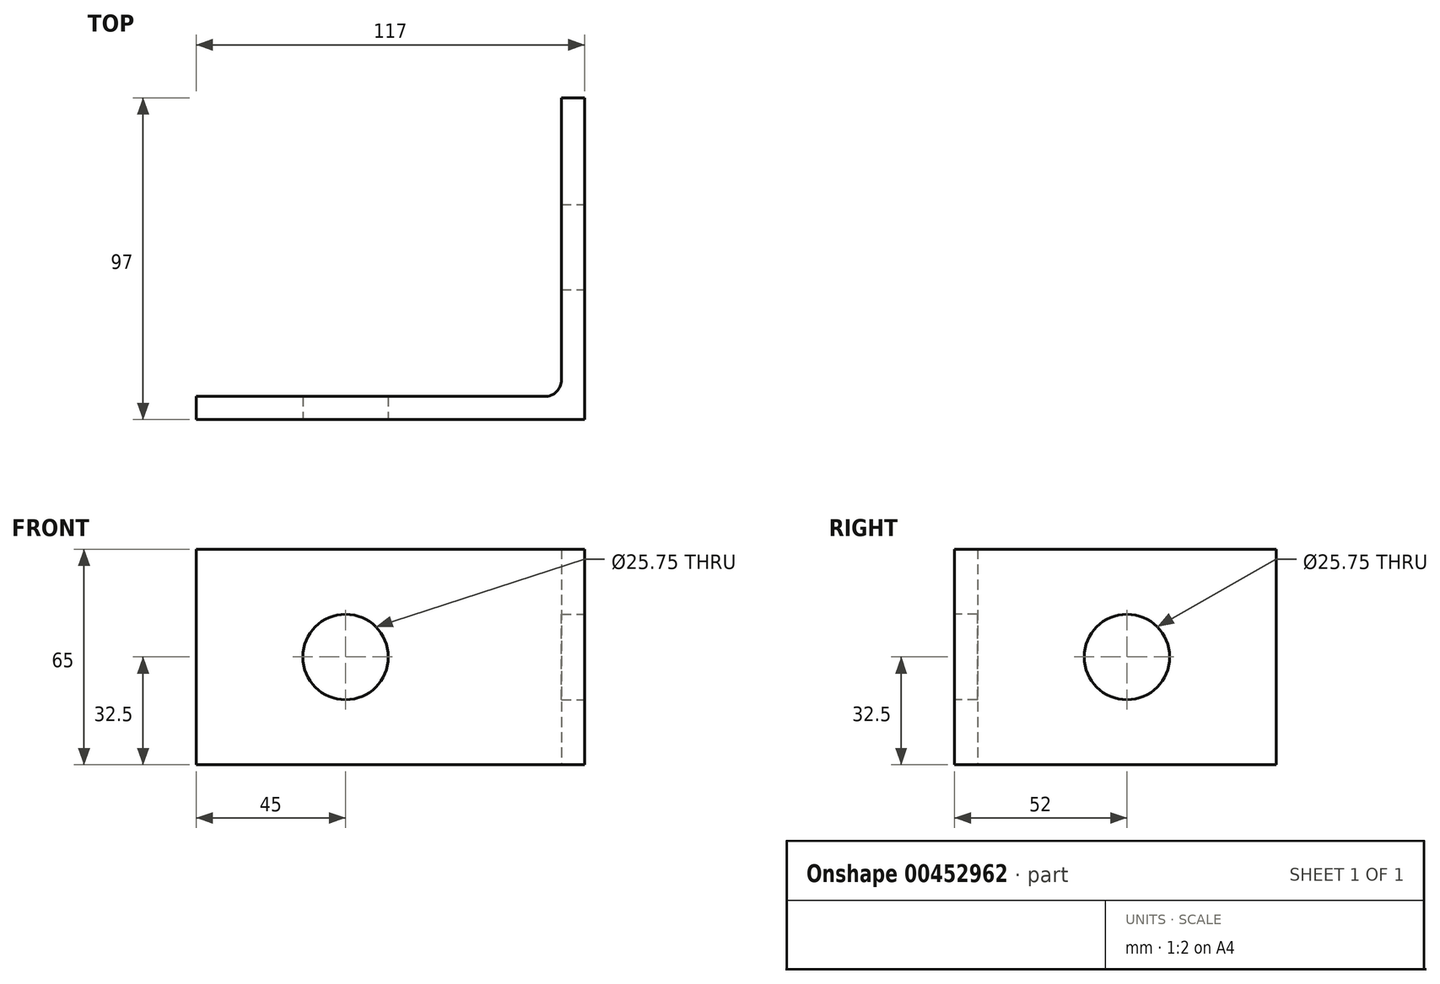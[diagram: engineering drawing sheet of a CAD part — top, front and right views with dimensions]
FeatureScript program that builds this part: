
annotation { "Feature Type Name" : "Feature", "Feature Type Description" : "" }
export const myFeature = defineFeature(function(context is Context, id is Id, definition is map)
    precondition{}
    {
        {
            var Q0;
            Q0=qCreatedBy(makeId("Top.planeOp"),FACE);
            var sketch = newSketch(context, id + "F0", { "sketchPlane" : qUnion([Q0])});
            skLineSegment(sketch, "E0", {"start": v(-110, 0) * mm, "end": v(-110, -7) * mm});
            skLineSegment(sketch, "E1", {"start": v(-110, -7) * mm, "end": v(7, -7) * mm});
            skLineSegment(sketch, "E2", {"start": v(7, -7) * mm, "end": v(7, 90) * mm});
            skLineSegment(sketch, "E3", {"start": v(7, 90) * mm, "end": v(0, 90) * mm});
            skLineSegment(sketch, "E4", {"start": v(0, 90) * mm, "end": v(0, 0) * mm});
            skLineSegment(sketch, "E5", {"start": v(0, 0) * mm, "end": v(-110, 0) * mm});
            skSolve(sketch);
        }
        {
            var Q0;
            Q0 = qSketchRegion(id + "F0", true);
            extrude(context, id + "F1", {"entities" : qUnion([Q0]), "depth" : 65 * mm});
        }
        {
            var Q0;
            Q0=makeQuery(id+"F1.opExtrude","SWEPT_EDGE",EDGE,{"disambiguationData":[OSD([sQuery(id+"F0.wireOp",EDGE,"E4"),sQuery(id+"F0.wireOp",EDGE,"E5")])]});
            fillet(context, id + "F2", {"entities" : qUnion([Q0]), "radius" : 5 * mm, "tangentPropagation" : true, "allowEdgeOverflow" : false});
        }
        {
            var Q0;
            Q0=makeQuery(id+"F1.opExtrude","SWEPT_FACE",FACE,{"disambiguationData":[OSD([sQuery(id+"F0.wireOp",EDGE,"E2")])]});
            var sketch = newSketch(context, id + "F3", { "sketchPlane" : qUnion([Q0])});
            skCircle(sketch, "E6", {"center": v(45, 32.5) * mm, "radius": 12.88 * mm});
            skPoint(sketch, "E6.centerSnap0", {"position": v(90, 32.5) * mm});
            skSolve(sketch);
        }
        {
            var Q0;
            Q0 = qSketchRegion(id + "F3", true);
            extrude(context, id + "F4", {"entities" : qUnion([Q0]), "operationType" : NewBodyOperationType.REMOVE, "oppositeDirection" : true, "depth" : 7 * mm});
        }
        {
            var Q0;
            Q0=makeQuery(id+"F1.opExtrude","SWEPT_FACE",FACE,{"disambiguationData":[OSD([sQuery(id+"F0.wireOp",EDGE,"E1")])]});
            var sketch = newSketch(context, id + "F5", { "sketchPlane" : qUnion([Q0])});
            skCircle(sketch, "E7", {"center": v(-65, 32.5) * mm, "radius": 12.88 * mm});
            skPoint(sketch, "E7.centerSnap0", {"position": v(-110, 32.5) * mm});
            skSolve(sketch);
        }
        {
            var Q0;
            Q0 = qSketchRegion(id + "F5", true);
            extrude(context, id + "F6", {"entities" : qUnion([Q0]), "operationType" : NewBodyOperationType.REMOVE, "oppositeDirection" : true, "depth" : 7 * mm});
        }
    });
